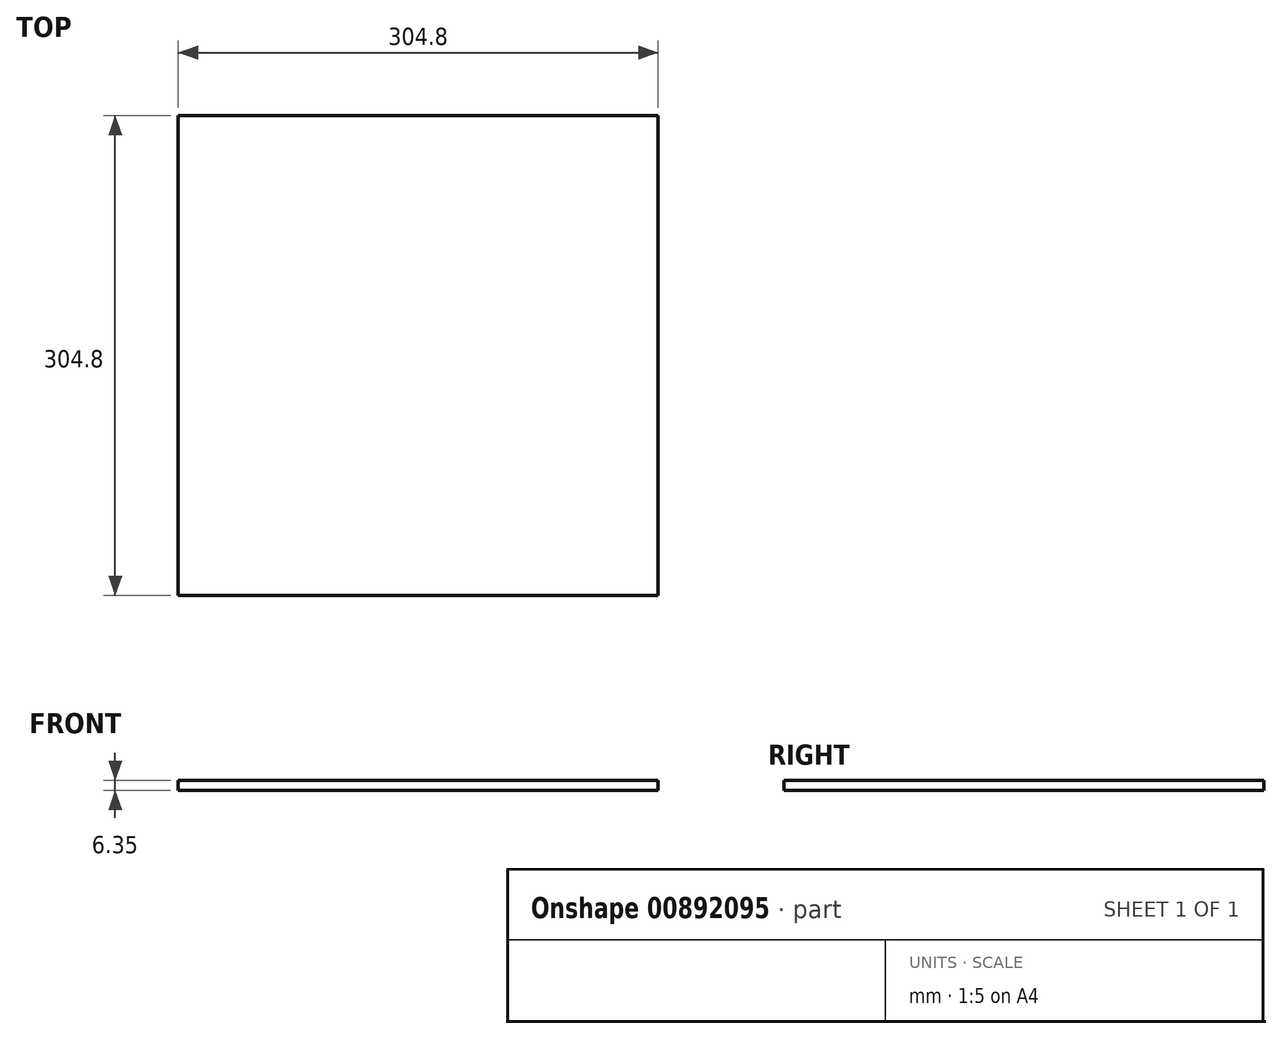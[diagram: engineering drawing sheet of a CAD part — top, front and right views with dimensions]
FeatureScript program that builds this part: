
annotation { "Feature Type Name" : "Feature", "Feature Type Description" : "" }
export const myFeature = defineFeature(function(context is Context, id is Id, definition is map)
    precondition{}
    {
        {
            var Q0;
            Q0=qCreatedBy(makeId("Top.planeOp"),FACE);
            var sketch = newSketch(context, id + "F0", { "sketchPlane" : qUnion([Q0])});
            skLineSegment(sketch, "E0.bottom", {"start": v(152.4, 152.4) * mm, "end": v(-152.4, 152.4) * mm});
            skLineSegment(sketch, "E0.top", {"start": v(152.4, -152.4) * mm, "end": v(-152.4, -152.4) * mm});
            skLineSegment(sketch, "E0.left", {"start": v(152.4, 152.4) * mm, "end": v(152.4, -152.4) * mm});
            skLineSegment(sketch, "E0.right", {"start": v(-152.4, 152.4) * mm, "end": v(-152.4, -152.4) * mm});
            skPoint(sketch, "E0.middle", {"position": v(0, 0) * mm});
            skSolve(sketch);
        }
        {
            var Q0;
            Q0 = qSketchRegion(id + "F0", true);
            extrude(context, id + "F1", {"entities" : qUnion([Q0]), "depth" : 6.35 * mm, "offsetDistance" : 25.4 * mm});
        }
    });
